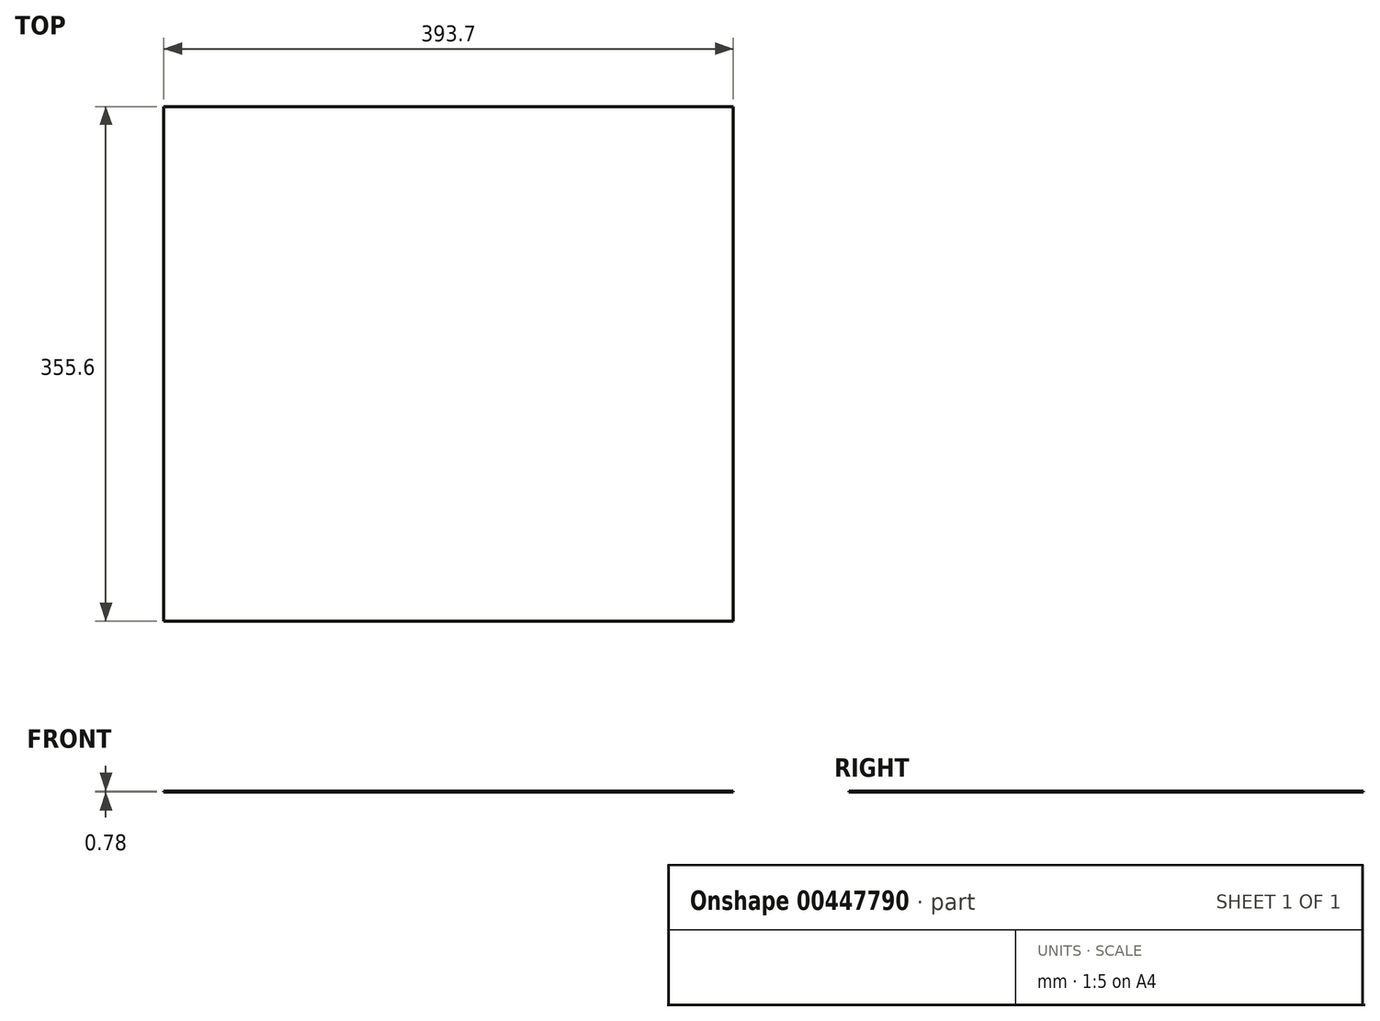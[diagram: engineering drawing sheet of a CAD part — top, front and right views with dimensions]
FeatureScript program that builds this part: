
annotation { "Feature Type Name" : "Feature", "Feature Type Description" : "" }
export const myFeature = defineFeature(function(context is Context, id is Id, definition is map)
    precondition{}
    {
        {
            var Q0;
            Q0=qCreatedBy(makeId("Top.planeOp"),FACE);
            var sketch = newSketch(context, id + "F0", { "sketchPlane" : qUnion([Q0])});
            skLineSegment(sketch, "E0.bottom", {"start": v(196.85, 177.8) * mm, "end": v(-196.85, 177.8) * mm});
            skLineSegment(sketch, "E0.top", {"start": v(196.85, -177.8) * mm, "end": v(-196.85, -177.8) * mm});
            skLineSegment(sketch, "E0.left", {"start": v(196.85, 177.8) * mm, "end": v(196.85, -177.8) * mm});
            skLineSegment(sketch, "E0.right", {"start": v(-196.85, 177.8) * mm, "end": v(-196.85, -177.8) * mm});
            skPoint(sketch, "E0.middle", {"position": v(0, 0) * mm});
            skSolve(sketch);
        }
        {
            var Q0;
            Q0=makeQuery(id+"F0.imprint","IMPRINT",FACE,{"disambiguationData":[TD([[makeQuery(id+"F0.imprint","IMPRINT",EDGE,{"derivedFrom":sQuery(id+"F0.wireOp",EDGE,"E0.bottom")}),1.0]])]});
            extrude(context, id + "F1", {"entities" : qUnion([Q0]), "depth" : 0.79 * mm, "offsetDistance" : 25.4 * mm, "symmetric" : true});
        }
    });
